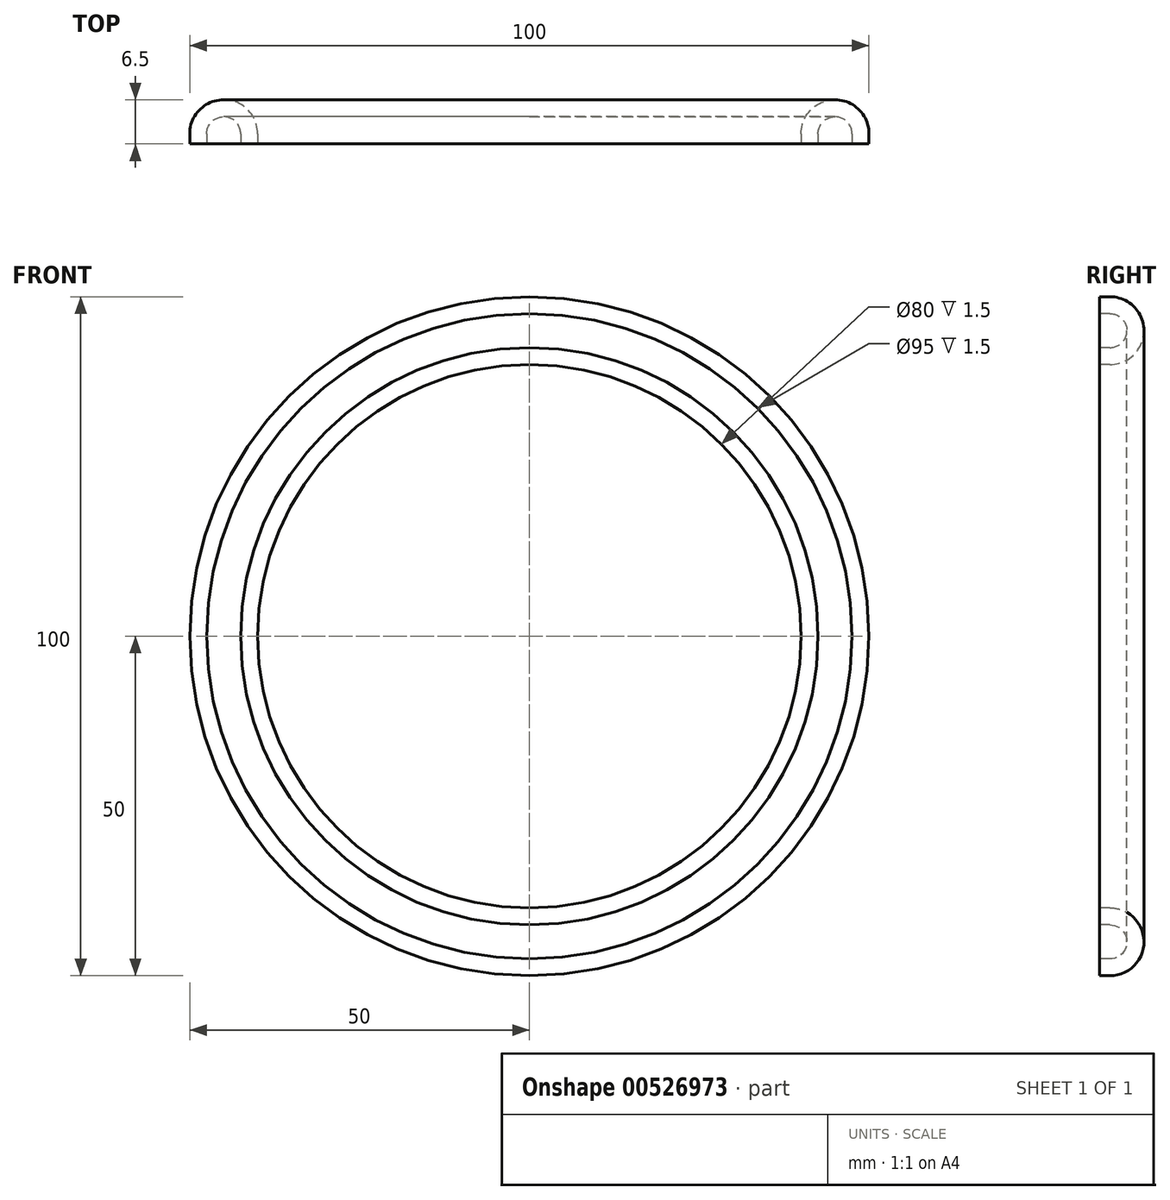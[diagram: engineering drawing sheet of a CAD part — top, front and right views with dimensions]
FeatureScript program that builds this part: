
annotation { "Feature Type Name" : "Feature", "Feature Type Description" : "" }
export const myFeature = defineFeature(function(context is Context, id is Id, definition is map)
    precondition{}
    {
        {
            var Q0;
            Q0=qCreatedBy(makeId("Front.planeOp"),FACE);
            var sketch = newSketch(context, id + "F0", { "sketchPlane" : qUnion([Q0])});
            skCircle(sketch, "E0", {"center": v(0, 0) * mm, "radius": 50 * mm});
            skSolve(sketch);
        }
        {
            var Q0;
            Q0=makeQuery(id+"F0.imprint","IMPRINT",FACE,{"disambiguationData":[TD([[makeQuery(id+"F0.imprint","IMPRINT",EDGE,{"derivedFrom":sQuery(id+"F0.wireOp",EDGE,"E0")}),1.0]])]});
            extrude(context, id + "F1", {"entities" : qUnion([Q0]), "oppositeDirection" : true, "depth" : 11.5 * mm, "offsetDistance" : 25 * mm});
        }
        {
            var Q0;
            Q0=sQuery(id+"F0.wireOp",VERTEX,"E0.center");
            var Q1;
            Q1=makeQuery(id+"F1.opExtrude","SWEPT_BODY",BODY,{"disambiguationData":[OSD([sQuery(id+"F0.wireOp",EDGE,"E0")])]});
            hole(context, id + "F2", {"style" : HoleStyle.SIMPLE, "endStyle" : HoleEndStyle.THROUGH, "holeDiameter" : 80 * mm, "isTappedThrough" : true, "tappedDepth" : 12 * mm, "tapClearance" : 3, "locations" : qUnion([Q0]), "scope" : qUnion([Q1])});
        }
        {
            var Q0;
            Q0=makeQuery(id+"F1.opExtrude","CAP_FACE",FACE,{"disambiguationData":[OSD([sQuery(id+"F0.wireOp",EDGE,"E0")])],"isStart":true});
            fillet(context, id + "F3", {"entities" : qUnion([Q0]), "radius" : 5 * mm, "tangentPropagation" : true, "allowEdgeOverflow" : false});
        }
        {
            var Q0;
            Q0=makeQuery(id+"F1.opExtrude","CAP_FACE",FACE,{"disambiguationData":[OSD([sQuery(id+"F0.wireOp",EDGE,"E0")])],"isStart":false});
            fillet(context, id + "F4", {"entities" : qUnion([Q0]), "radius" : 5 * mm, "tangentPropagation" : true, "allowEdgeOverflow" : false});
        }
        {
            var Q0;
            Q0=makeQuery(id+"F3.opFillet","BLEND_FACE",FACE,{"disambiguationData":[OSD([sQuery(id+"F0.wireOp",EDGE,"E0")])]});
            shell(context, id + "F5", {"entities" : qUnion([Q0]), "thickness" : 2.5 * mm});
        }
    });
